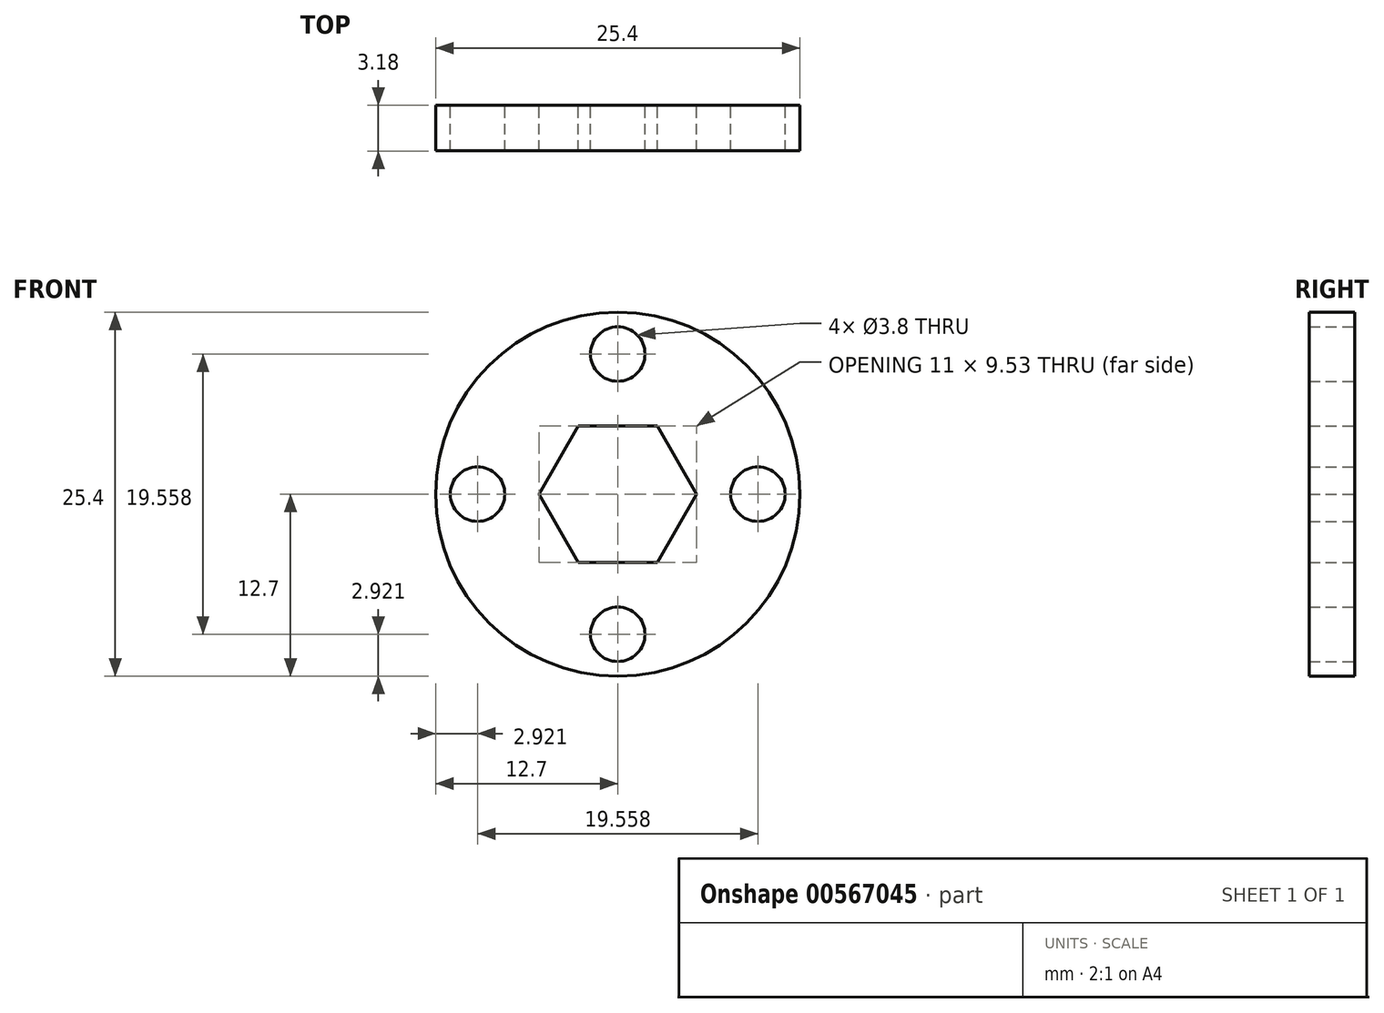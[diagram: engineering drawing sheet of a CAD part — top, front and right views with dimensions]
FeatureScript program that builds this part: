
annotation { "Feature Type Name" : "Feature", "Feature Type Description" : "" }
export const myFeature = defineFeature(function(context is Context, id is Id, definition is map)
    precondition{}
    {
        {
            var Q0;
            Q0=qCreatedBy(makeId("Front.planeOp"),FACE);
            var sketch = newSketch(context, id + "F0", { "sketchPlane" : qUnion([Q0])});
            skCircle(sketch, "E0", {"center": v(0, 0) * mm, "radius": 12.7 * mm});
            skCircle(sketch, "E1.cCircle", {"center": v(0, 0) * mm, "radius": 4.76 * mm, "construction": true});
            skLineSegment(sketch, "E1.0", {"start": v(-2.75, 4.76) * mm, "end": v(2.75, 4.76) * mm});
            skLineSegment(sketch, "E1.1", {"start": v(2.75, 4.76) * mm, "end": v(5.5, 0) * mm});
            skLineSegment(sketch, "E1.2", {"start": v(5.5, 0) * mm, "end": v(2.75, -4.76) * mm});
            skLineSegment(sketch, "E1.3", {"start": v(2.75, -4.76) * mm, "end": v(-2.75, -4.76) * mm});
            skLineSegment(sketch, "E1.4", {"start": v(-2.75, -4.76) * mm, "end": v(-5.5, 0) * mm});
            skLineSegment(sketch, "E1.5", {"start": v(-5.5, 0) * mm, "end": v(-2.75, 4.76) * mm});
            skPoint(sketch, "E1.0.midPoint", {"position": v(0, 4.76) * mm});
            skCircle(sketch, "E2", {"center": v(0, 9.78) * mm, "radius": 1.9 * mm});
            skCircle(sketch, "E3.MirrorC", {"center": v(0, -9.78) * mm, "radius": 1.9 * mm});
            skCircle(sketch, "E4.1.0", {"center": v(9.78, 0) * mm, "radius": 1.9 * mm});
            skCircle(sketch, "E4.3.0", {"center": v(-9.78, 0) * mm, "radius": 1.9 * mm});
            skLineSegment(sketch, "E4.anchor1", {"start": v(0, 0) * mm, "end": v(0, 9.78) * mm, "construction": true});
            skLineSegment(sketch, "E4.anchor2", {"start": v(0, 0) * mm, "end": v(-9.78, 0) * mm, "construction": true});
            skSolve(sketch);
        }
        {
            var Q0;
            Q0 = qSketchRegion(id + "F0", true);
            extrude(context, id + "F1", {"entities" : qUnion([Q0]), "depth" : 3.17 * mm, "offsetDistance" : 25.4 * mm});
        }
    });
